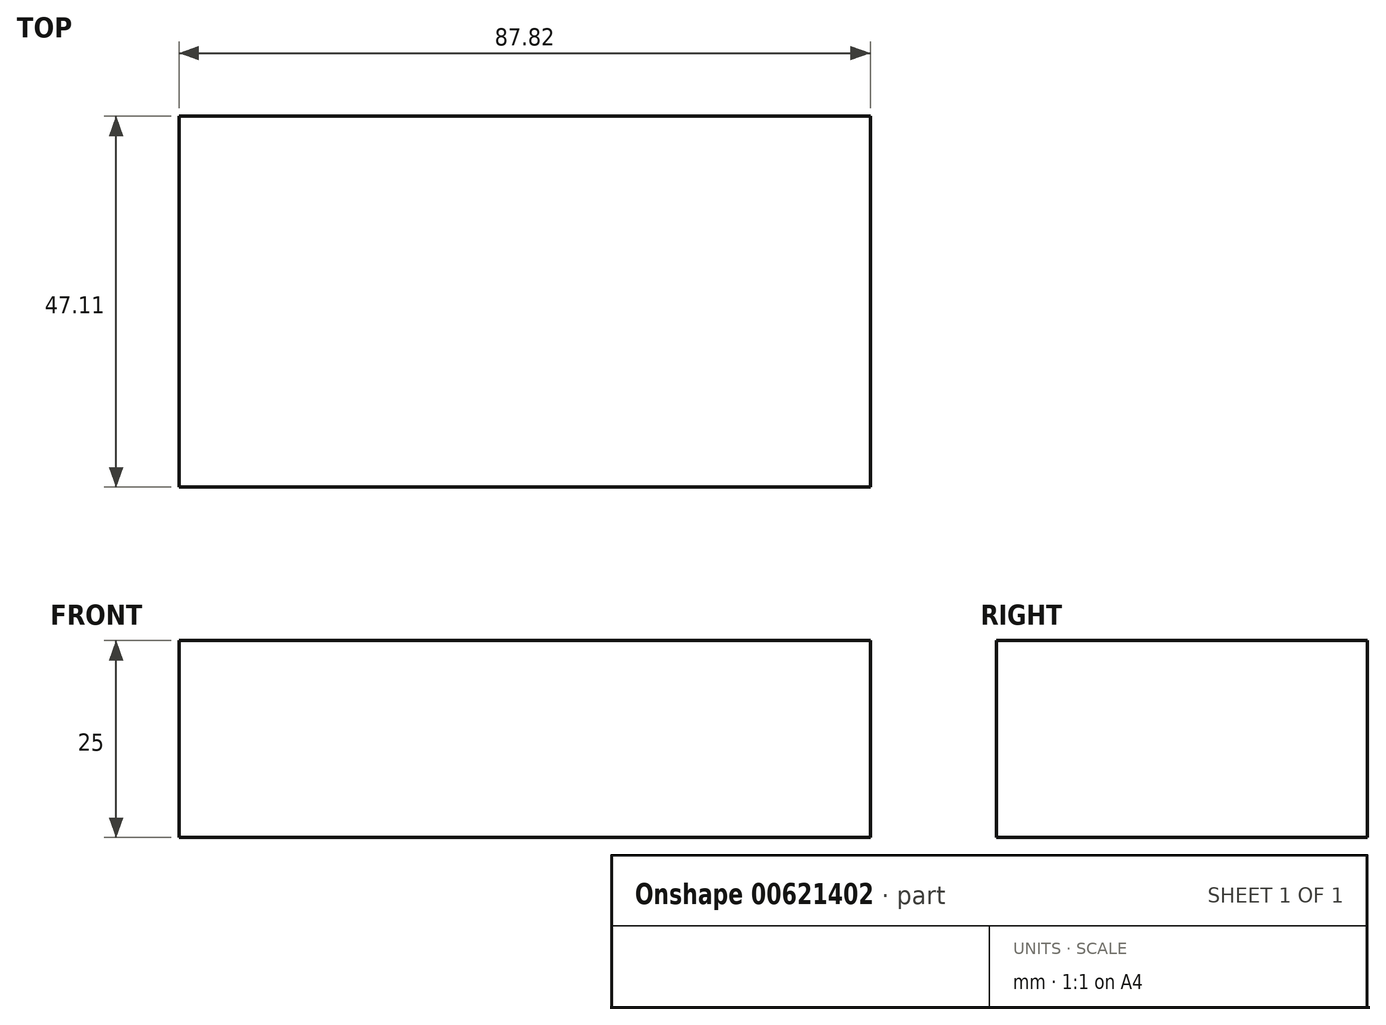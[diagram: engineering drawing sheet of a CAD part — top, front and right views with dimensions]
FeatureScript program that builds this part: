
annotation { "Feature Type Name" : "Feature", "Feature Type Description" : "" }
export const myFeature = defineFeature(function(context is Context, id is Id, definition is map)
    precondition{}
    {
        {
            var Q0;
            Q0=qCreatedBy(makeId("Top.planeOp"),FACE);
            var sketch = newSketch(context, id + "F0", { "sketchPlane" : qUnion([Q0])});
            skLineSegment(sketch, "E0.bottom", {"start": v(-100.82, 10.06) * mm, "end": v(-13, 10.06) * mm});
            skLineSegment(sketch, "E0.top", {"start": v(-100.82, -37.05) * mm, "end": v(-13, -37.05) * mm});
            skLineSegment(sketch, "E0.left", {"start": v(-100.82, 10.06) * mm, "end": v(-100.82, -37.05) * mm});
            skLineSegment(sketch, "E0.right", {"start": v(-13, 10.06) * mm, "end": v(-13, -37.05) * mm});
            skSolve(sketch);
        }
        {
            var Q0;
            Q0=makeQuery(id+"F0.imprint","IMPRINT",FACE,{"disambiguationData":[TD([[makeQuery(id+"F0.imprint","IMPRINT",EDGE,{"derivedFrom":sQuery(id+"F0.wireOp",EDGE,"E0.bottom")}),-1.0]])]});
            extrude(context, id + "F1", {"entities" : qUnion([Q0]), "depth" : 25 * mm, "offsetDistance" : 25 * mm});
        }
    });
